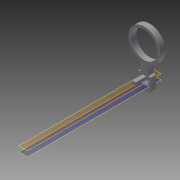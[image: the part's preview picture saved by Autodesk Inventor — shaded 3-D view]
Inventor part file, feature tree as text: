
AUTODESK INVENTOR PART (.ipt)
format: ipt  version: 2015 SP1 (Build 190203100, 203)  size: 210,432 bytes
history: native  units: mm
features: extrude x5, sketch x5, reference x5, projected_geometry x5, plane x2, fillet x2, other x1
ambient origin geometry x8: Origin, YZ Plane, XZ Plane, XY Plane, X Axis, Y Axis, Z Axis, Center Point
bodies: Body1 (feature_tree)
feature tree (25):
  other  "Sólido1"
  plane  "Plano de trabajo1"
  extrude  "Extrusión1"  Depth=30.0mm TaperAngle=0.0deg
  plane  "Plano de trabajo2"
  extrude  "Extrusión2"  Depth=2.5mm
  extrude  "Extrusión3"  Depth=5.0mm
  extrude  "Extrusión4"  Depth=25.0mm
  fillet  "Empalme1"  Radius=25.0mm
  extrude  "Extrusión5"  Depth=2.0mm
  fillet  "Empalme2"  Radius=25.0mm
  sketch  "Boceto1"  dims[d0=10.0mm d1=30.0mm d2=0.0mm]
  reference  "Referencia1"
  reference  "Referencia2"
  reference  "Referencia3"
  sketch  "Boceto2"  dims[d3=10.0mm d4=0.0mm d5=2.5mm]
  projected_geometry  "Contorno proyectado1"
  reference  "Referencia4"
  sketch  "Boceto3"  dims[d6=7.0mm d7=5.0mm]
  projected_geometry  "Contorno proyectado2"
  sketch  "Boceto4"  dims[d8=20.0mm d9=0.0mm d10=25.0mm d11=25.0mm]
  projected_geometry  "Contorno proyectado3"
  projected_geometry  "Contorno proyectado4"
  reference  "Referencia5"
  sketch  "Boceto5"  dims[d12=20.0mm d13=0.0mm d14=2.0mm d15=25.0mm d16=90.0deg d17=60.0mm d18=20.0mm d19=0.0mm d20=2.0mm]
  projected_geometry  "Contorno proyectado5"
